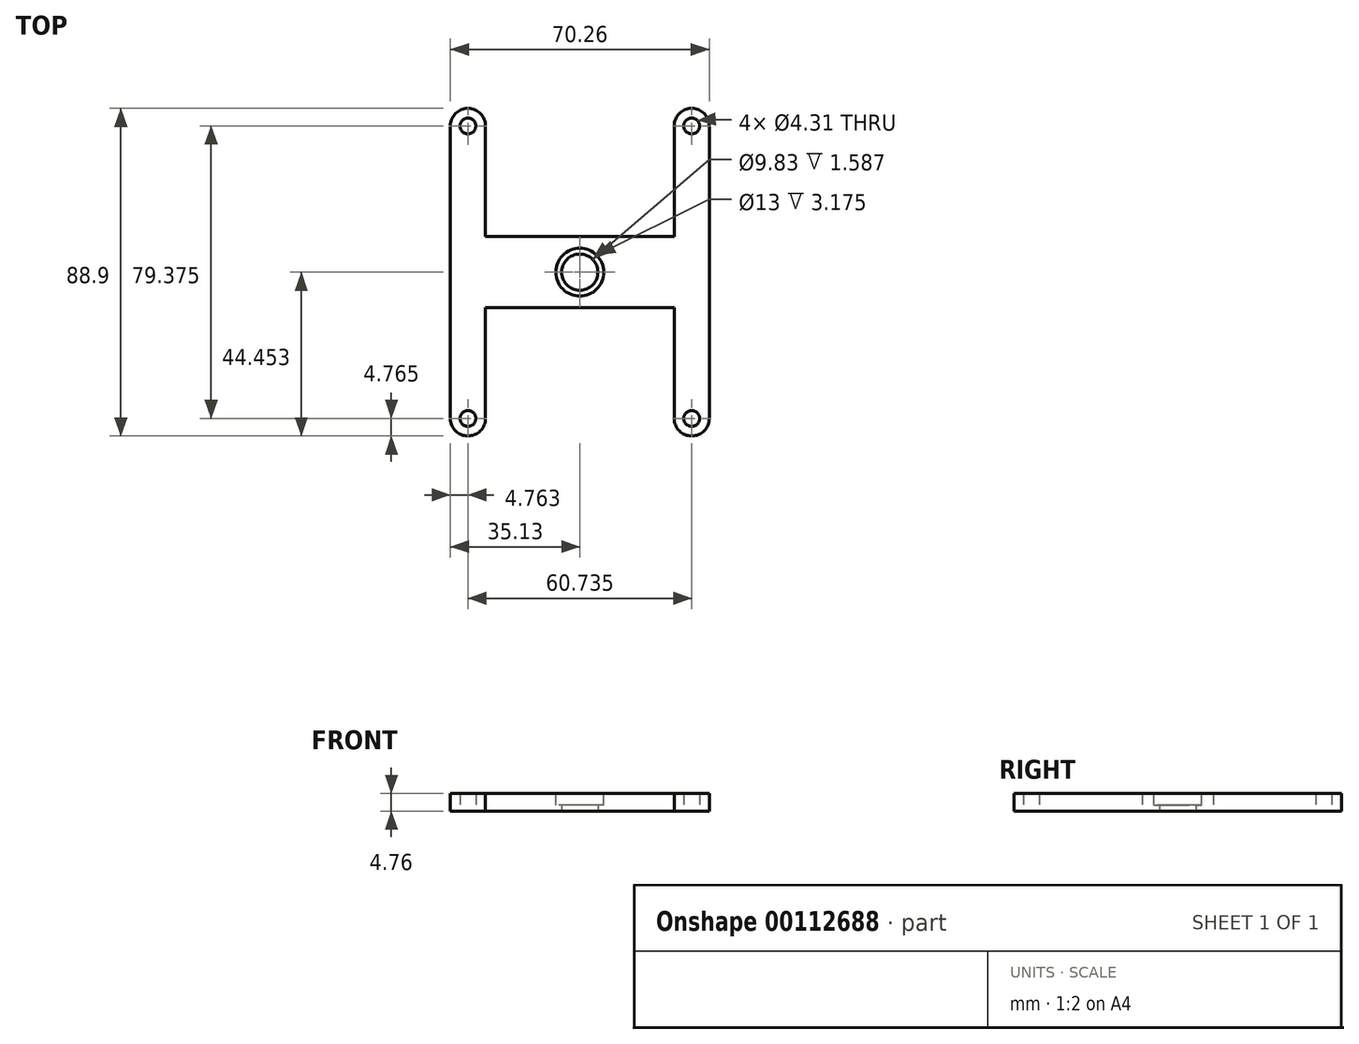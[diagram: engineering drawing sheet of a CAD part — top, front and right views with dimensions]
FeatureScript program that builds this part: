
annotation { "Feature Type Name" : "Feature", "Feature Type Description" : "" }
export const myFeature = defineFeature(function(context is Context, id is Id, definition is map)
    precondition{}
    {
        {
            var Q0;
            Q0=qCreatedBy(makeId("Top.planeOp"),FACE);
            var sketch = newSketch(context, id + "F0", { "sketchPlane" : qUnion([Q0])});
            skLineSegment(sketch, "E0.bottom", {"start": v(0, 0) * mm, "end": v(9.53, 0) * mm, "construction": true});
            skLineSegment(sketch, "E0.top", {"start": v(0, -79.38) * mm, "end": v(9.52, -79.38) * mm, "construction": true});
            skLineSegment(sketch, "E0.left", {"start": v(0, 0) * mm, "end": v(0, -79.38) * mm});
            skLineSegment(sketch, "E1", {"start": v(9.53, 0) * mm, "end": v(9.53, -30.01) * mm});
            skLineSegment(sketch, "E2", {"start": v(9.53, -79.38) * mm, "end": v(9.53, -49.36) * mm});
            skLineSegment(sketch, "E3.bottom", {"start": v(9.52, -30.01) * mm, "end": v(60.74, -30.01) * mm});
            skLineSegment(sketch, "E3.top", {"start": v(9.52, -49.36) * mm, "end": v(60.74, -49.36) * mm});
            skLineSegment(sketch, "E3.left", {"start": v(9.53, -30.01) * mm, "end": v(9.53, -49.36) * mm, "construction": true});
            skLineSegment(sketch, "E3.right", {"start": v(60.74, -30.01) * mm, "end": v(60.74, -49.36) * mm, "construction": true});
            skLineSegment(sketch, "E4.bottom", {"start": v(60.74, 0) * mm, "end": v(70.26, 0) * mm, "construction": true});
            skLineSegment(sketch, "E4.top", {"start": v(60.74, -79.38) * mm, "end": v(70.26, -79.38) * mm, "construction": true});
            skLineSegment(sketch, "E4.right", {"start": v(70.26, 0) * mm, "end": v(70.26, -79.38) * mm});
            skLineSegment(sketch, "E5", {"start": v(60.74, -30.01) * mm, "end": v(60.74, 0) * mm});
            skLineSegment(sketch, "E6", {"start": v(60.74, -49.36) * mm, "end": v(60.74, -79.38) * mm});
            skArc(sketch, "E7", {"start": v(9.53, 0) * mm, "mid": v(4.76, 4.76) * mm, "end": v(0, 0) * mm});
            skArc(sketch, "E8", {"start": v(70.26, 0) * mm, "mid": v(65.5, 4.76) * mm, "end": v(60.74, 0) * mm});
            skArc(sketch, "E9", {"start": v(60.74, -79.38) * mm, "mid": v(65.5, -84.14) * mm, "end": v(70.26, -79.38) * mm});
            skArc(sketch, "E10", {"start": v(0, -79.38) * mm, "mid": v(4.76, -84.14) * mm, "end": v(9.52, -79.38) * mm});
            skCircle(sketch, "E11", {"center": v(4.76, 0) * mm, "radius": 2.15 * mm});
            skCircle(sketch, "E12", {"center": v(65.5, 0) * mm, "radius": 2.15 * mm});
            skCircle(sketch, "E13", {"center": v(65.5, -79.38) * mm, "radius": 2.15 * mm});
            skCircle(sketch, "E14", {"center": v(4.76, -79.38) * mm, "radius": 2.15 * mm});
            skLineSegment(sketch, "E15", {"start": v(9.53, -39.69) * mm, "end": v(60.74, -39.69) * mm, "construction": true});
            skCircle(sketch, "E16", {"center": v(35.13, -39.69) * mm, "radius": 4.91 * mm});
            skSolve(sketch);
        }
        {
            var Q0;
            Q0 = qSketchRegion(id + "F0", true);
            extrude(context, id + "F1", {"entities" : qUnion([Q0]), "depth" : 4.76 * mm});
        }
        {
            var Q0;
            Q0=makeQuery(id+"F1.opExtrude","CAP_FACE",FACE,{"disambiguationData":[OSD([sQuery(id+"F0.wireOp",EDGE,"E0.left"),sQuery(id+"F0.wireOp",EDGE,"E1"),sQuery(id+"F0.wireOp",EDGE,"E2"),sQuery(id+"F0.wireOp",EDGE,"E3.bottom"),sQuery(id+"F0.wireOp",EDGE,"E3.top"),sQuery(id+"F0.wireOp",EDGE,"E4.right"),sQuery(id+"F0.wireOp",EDGE,"E5"),sQuery(id+"F0.wireOp",EDGE,"E6"),sQuery(id+"F0.wireOp",EDGE,"E7"),sQuery(id+"F0.wireOp",EDGE,"E8"),sQuery(id+"F0.wireOp",EDGE,"E9"),sQuery(id+"F0.wireOp",EDGE,"E10"),sQuery(id+"F0.wireOp",EDGE,"E11"),sQuery(id+"F0.wireOp",EDGE,"E12"),sQuery(id+"F0.wireOp",EDGE,"E13"),sQuery(id+"F0.wireOp",EDGE,"E14"),sQuery(id+"F0.wireOp",EDGE,"E16")])],"isStart":false});
            var sketch = newSketch(context, id + "F2", { "sketchPlane" : qUnion([Q0])});
            skCircle(sketch, "E17", {"center": v(35.13, -39.69) * mm, "radius": 6.5 * mm});
            skSolve(sketch);
        }
        {
            var Q0;
            Q0 = qSketchRegion(id + "F2", true);
            extrude(context, id + "F3", {"entities" : qUnion([Q0]), "operationType" : NewBodyOperationType.REMOVE, "oppositeDirection" : true, "depth" : 3.17 * mm});
        }
    });
